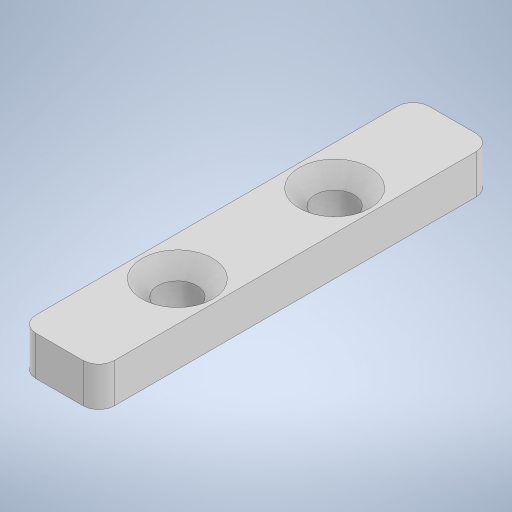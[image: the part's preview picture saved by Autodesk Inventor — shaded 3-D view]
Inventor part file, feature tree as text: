
AUTODESK INVENTOR PART (.ipt)
format: ipt  version: 2023 (Build 270158000, 158)  size: 234,496 bytes
history: native  units: in
note: dims shown in document units (in); Inventor stores cm internally (conversion verified against a paired STEP export)
features: extrude x1, fillet x1, chamfer x1, sketch x1
ambient origin geometry x8: Origin, YZ Plane, XZ Plane, XY Plane, X Axis, Y Axis, Z Axis, Center Point
bodies: Solid1 (feature_tree)
feature tree (4):
  extrude  "Extrusion1"  Depth=0.1969in
  fillet  "Fillet1"  Radius=0.3937in
  chamfer  "Chamfer1"  Distance=1.9685in
  sketch  "Sketch1"  dims[d0=0.3937in d1=0.1969in d2=0.3937in d3=1.9685in d4=0.1969in d5=0.0in d6=0.0787in d7=0.0787in d8=0.0787in d9=45.0deg]
